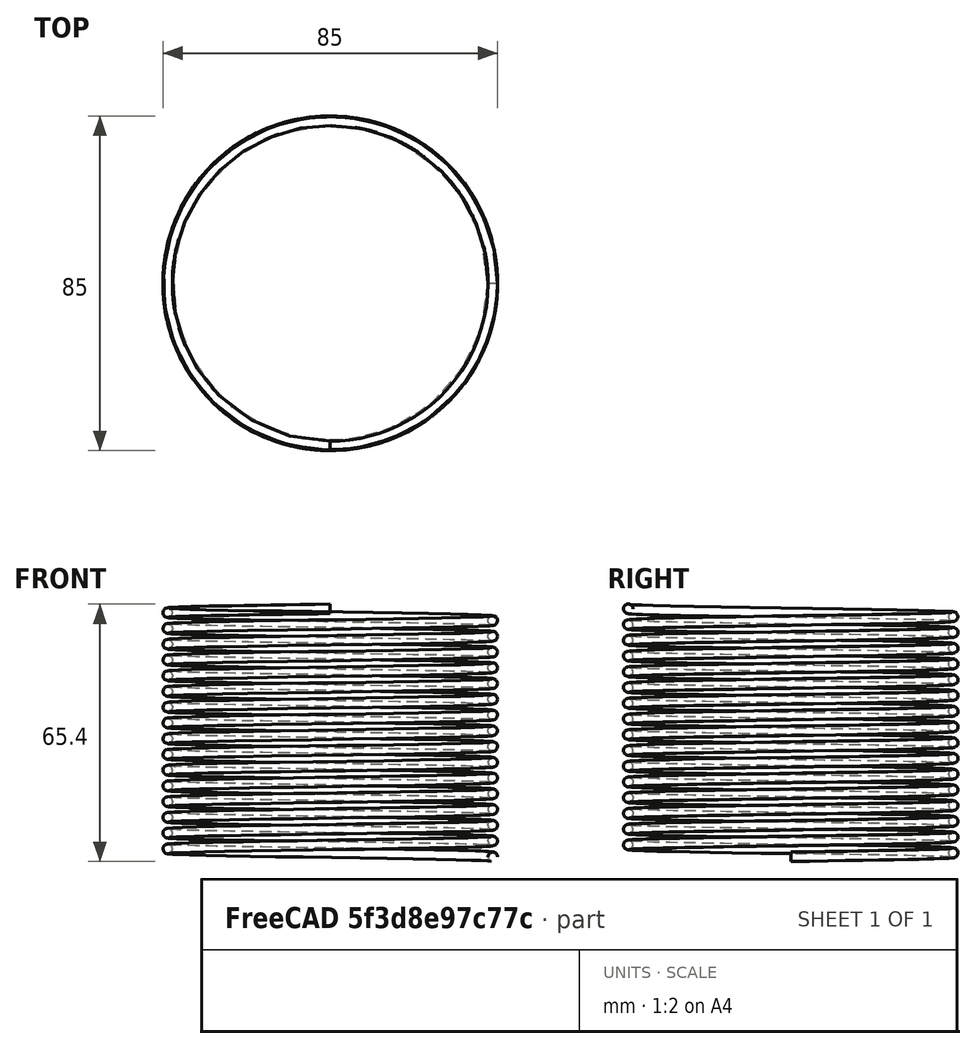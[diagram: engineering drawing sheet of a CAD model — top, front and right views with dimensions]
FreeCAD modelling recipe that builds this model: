
FCSTD DOCUMENT  (FreeCAD 0.19R24291 (Git))
Label: x_pod_motor
License: All rights reserved
LicenseURL: http://en.wikipedia.org/wiki/All_rights_reserved
objects: Part::FeaturePython×2, Part::Helix×1, PartDesign::FeatureBase×1, Sketcher::SketchObject×1, Part::Sweep×1, PartDesign::Body×1, Part::Box×1, Part::MultiFuse×1
note: 9 computed .brp shape members not serialized (recipe doc carries the construction recipe); baked Part::Feature solids carry a one-line shape summary decoded from their .brp

FEATURE [Part::Helix] Helix001  label="Helix_out"
  Angle = 0
  AttacherType = Attacher::AttachEngine3D
  Height = 63
  LocalCoord = 0
  Pitch = 4
  Radius = 41.3
  Style = 1
FEATURE [PartDesign::FeatureBase] BaseFeature001
  BaseFeature = -> Helix001
FEATURE [Sketcher::SketchObject] Sketch001
  ExternalGeometry = -> [BaseFeature001]
  FullyConstrained = true
  MapMode = 5
  Placement = pos=(0,0,0) rot=(1,0,0;1.5708rad)
  Support = -> [XZ_Plane001]
  sketch-geometry (1):
    g0: Circle CenterX=41.3 CenterY=0 CenterZ=0 NormalX=0 NormalY=0 NormalZ=1 AngleXU=0 Radius=1.2
  constraints (2):
    c: Radius(g0) = 1.2
    c: Coincident(g0,g-3)
FEATURE [Part::Sweep] Sweep001  label="Sweep_out"
  Frenet = true
  Placement = pos=(0,0,-34) rot=(0,0,1;0rad)
  Sections = -> [Sketch001]
  Solid = true
  Spine = -> BaseFeature001 [Edge1,Edge2,Edge3,Edge4,Edge5,Edge6,Edge7,Edge8,Edge9,Edge10,Edge11,Edge12,Edge13,Edge14,Edge15,Edge16]
  Transition = 1
FEATURE [PartDesign::Body] Body001
  BaseFeature = -> Helix001
  Group = -> [BaseFeature001,Sketch001]
  Origin = -> Origin001
  Tip = -> BaseFeature001
FEATURE [Part::FeaturePython] Tube  # WARN: FeaturePython — macro-defined, semantics opaque (R4)
  AttacherType = Attacher::AttachEngine3D
  Height = 20
  InnerRadius = 40
  OuterRadius = 41.5
  Placement = pos=(0,0,-31) rot=(0,0,1;0rad)
FEATURE [Part::FeaturePython] Tube001  # WARN: FeaturePython — macro-defined, semantics opaque (R4)
  AttacherType = Attacher::AttachEngine3D
  Height = 2
  InnerRadius = 25
  OuterRadius = 43
  Placement = pos=(0,0,-31) rot=(0,0,1;0rad)
FEATURE [Part::Box] Box  label="Cube"
  AttacherType = Attacher::AttachEngine3D
  Height = 2
  Length = 10
  Placement = pos=(-5,-30,-31) rot=(0,0,1;0rad)
  Width = 59
FEATURE [Part::MultiFuse] Fusion001
  Shapes = -> [Tube,Tube001,Box,Sweep001]
